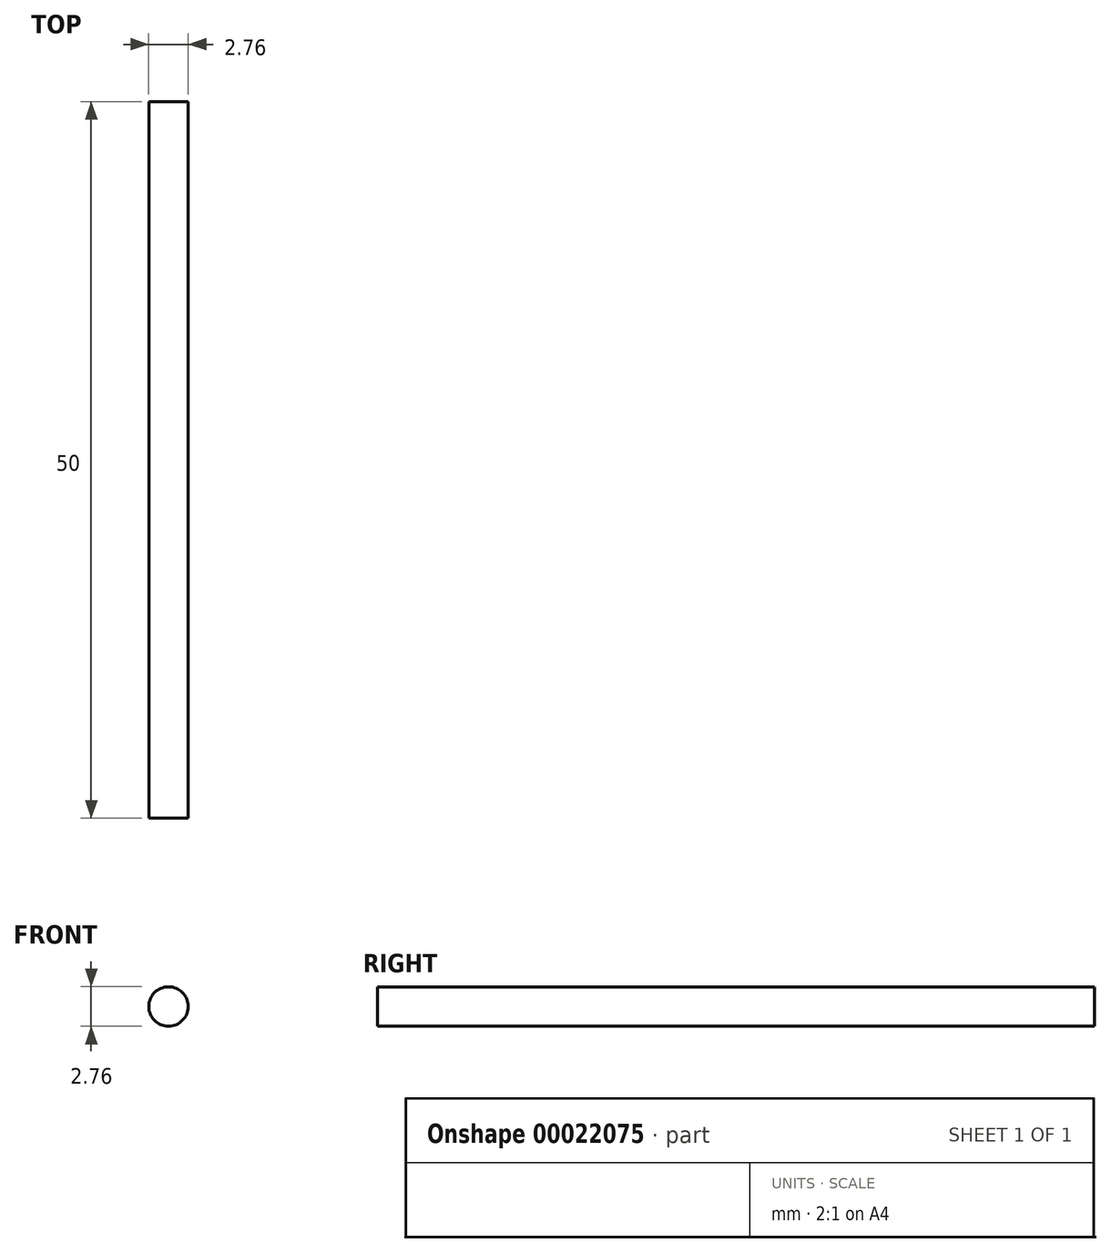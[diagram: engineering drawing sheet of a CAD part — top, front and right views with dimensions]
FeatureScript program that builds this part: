
annotation { "Feature Type Name" : "Feature", "Feature Type Description" : "" }
export const myFeature = defineFeature(function(context is Context, id is Id, definition is map)
    precondition{}
    {
        {
            var Q0;
            Q0=qCreatedBy(makeId("Front.planeOp"),FACE);
            var sketch = newSketch(context, id + "F0", { "sketchPlane" : qUnion([Q0])});
            skCircle(sketch, "E0", {"center": v(0, 0) * mm, "radius": 1.38 * mm});
            skSolve(sketch);
        }
        {
            var Q0;
            Q0 = qSketchRegion(id + "F0", true);
            extrude(context, id + "F1", {"entities" : qUnion([Q0]), "depth" : 50 * mm});
        }
    });
